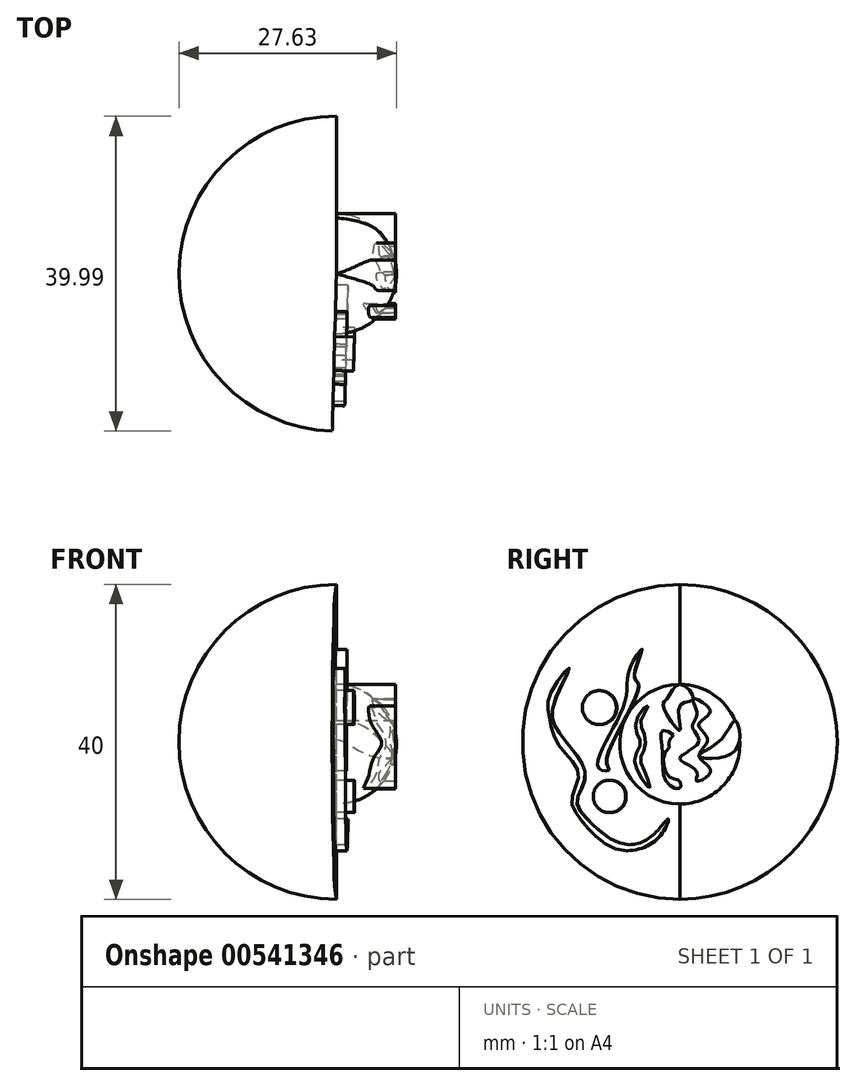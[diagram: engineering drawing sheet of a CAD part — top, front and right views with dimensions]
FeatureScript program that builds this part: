
annotation { "Feature Type Name" : "Feature", "Feature Type Description" : "" }
export const myFeature = defineFeature(function(context is Context, id is Id, definition is map)
    precondition{}
    {
        {
            var Q0;
            Q0=qCreatedBy(makeId("Right.planeOp"),FACE);
            var sketch = newSketch(context, id + "F0", { "sketchPlane" : qUnion([Q0])});
            skLineSegment(sketch, "E0", {"start": v(0, 0) * mm, "end": v(0, 40) * mm});
            skArc(sketch, "E1", {"start": v(0, 40) * mm, "mid": v(20, 20) * mm, "end": v(0, 0) * mm});
            skSolve(sketch);
        }
        {
            var Q0;
            Q0 = qSketchRegion(id + "F0", true);
            var Q1;
            Q1=sQuery(id+"F0.wireOp",EDGE,"E0");
            revolve(context, id + "F1", {"entities" : qUnion([Q0]), "axis" : qUnion([Q1]), "revolveType" : RevolveType.ONE_DIRECTION, "angle" : 178.48 * degree});
        }
        {
            var Q0;
            Q0=makeQuery(id+"F1.opRevolve","CAP_FACE",FACE,{"disambiguationData":[OSD([sQuery(id+"F0.wireOp",EDGE,"E0"),sQuery(id+"F0.wireOp",EDGE,"E1")])],"isStart":true});
            var sketch = newSketch(context, id + "F2", { "sketchPlane" : qUnion([Q0])});
            skLineSegment(sketch, "E2", {"start": v(0, 12.12) * mm, "end": v(0, 27.3) * mm});
            skArc(sketch, "E3", {"start": v(0, 12.12) * mm, "mid": v(7.63, 19.71) * mm, "end": v(0, 27.3) * mm});
            skSolve(sketch);
        }
        {
            var Q0;
            Q0=makeQuery(id+"F2.imprint","IMPRINT",FACE,{"disambiguationData":[TD([[makeQuery(id+"F2.imprint","IMPRINT",EDGE,{"derivedFrom":sQuery(id+"F2.wireOp",EDGE,"E2")}),-1.0]])]});
            var Q1;
            Q1=sQuery(id+"F2.wireOp",EDGE,"E2");
            revolve(context, id + "F3", {"operationType" : NewBodyOperationType.ADD, "entities" : qUnion([Q0]), "axis" : qUnion([Q1]), "revolveType" : RevolveType.FULL});
        }
        {
            var Q0;
            Q0=makeQuery(id+"F1.opRevolve","CAP_FACE",FACE,{"disambiguationData":[OSD([sQuery(id+"F0.wireOp",EDGE,"E0"),sQuery(id+"F0.wireOp",EDGE,"E1")])],"isStart":false});
            var sketch = newSketch(context, id + "F4", { "sketchPlane" : qUnion([Q0])});
            skCircle(sketch, "E4", {"center": v(-8.87, 13.08) * mm, "radius": 2.06 * mm});
            skSolve(sketch);
        }
        {
            var Q0;
            Q0=makeQuery(id+"F4.imprint","IMPRINT",FACE,{"disambiguationData":[TD([[makeQuery(id+"F4.imprint","IMPRINT",EDGE,{"derivedFrom":sQuery(id+"F4.wireOp",EDGE,"E4")}),1.0]])]});
            extrude(context, id + "F5", {"entities" : qUnion([Q0]), "operationType" : NewBodyOperationType.ADD, "depth" : 2.5 * mm, "offsetDistance" : 25 * mm});
        }
        {
            var Q0;
            Q0=makeQuery(id+"F1.opRevolve","CAP_FACE",FACE,{"disambiguationData":[OSD([sQuery(id+"F0.wireOp",EDGE,"E0"),sQuery(id+"F0.wireOp",EDGE,"E1")])],"isStart":false});
            var sketch = newSketch(context, id + "F6", { "sketchPlane" : qUnion([Q0])});
            skCircle(sketch, "E5", {"center": v(-10.16, 24.36) * mm, "radius": 2.16 * mm});
            skSolve(sketch);
        }
        {
            var Q0;
            Q0=makeQuery(id+"F6.imprint","IMPRINT",FACE,{"disambiguationData":[TD([[makeQuery(id+"F6.imprint","IMPRINT",EDGE,{"derivedFrom":sQuery(id+"F6.wireOp",EDGE,"E5")}),1.0]])]});
            extrude(context, id + "F7", {"entities" : qUnion([Q0]), "operationType" : NewBodyOperationType.ADD, "depth" : 2.5 * mm, "offsetDistance" : 25 * mm});
        }
        {
            var Q0;
            Q0=makeQuery(id+"F1.opRevolve","CAP_FACE",FACE,{"disambiguationData":[OSD([sQuery(id+"F0.wireOp",EDGE,"E0"),sQuery(id+"F0.wireOp",EDGE,"E1")])],"isStart":true});
            var sketch = newSketch(context, id + "F8", { "sketchPlane" : qUnion([Q0])});
            skFitSpline(sketch, "E6", {"points": [v(1.7, 25.46) * mm, v(3.87, 23.89) * mm, v(2.4, 22.22) * mm, v(3.52, 20.3) * mm, v(2.44, 18.2) * mm, v(3.92, 16.28) * mm, v(2.15, 15) * mm, v(2.15, 16.23) * mm, v(0, 17.9) * mm, v(2.4, 19.96) * mm, v(1.6, 21.92) * mm, v(2.2, 23.6) * mm, v(1.7, 25.46) * mm]});
            skFitSpline(sketch, "E7", {"points": [v(-4.04, 24.58) * mm, v(-5.22, 23.45) * mm, v(-5.46, 21.19) * mm, v(-4.97, 19.81) * mm, v(-5.7, 18.1) * mm, v(-4.92, 15.54) * mm, v(-3.84, 14.12) * mm, v(-4.24, 15.74) * mm, v(-5.02, 17.85) * mm, v(-4.48, 19.08) * mm, v(-4.58, 21.19) * mm, v(-4.92, 22.66) * mm, v(-4.04, 24.58) * mm]});
            skFitSpline(sketch, "E8", {"points": [v(-2.12, 21.43) * mm, v(0, 20) * mm, v(-1.58, 19.08) * mm, v(-1.48, 15.74) * mm, v(0, 15) * mm, v(0, 14.12) * mm, v(-1.73, 15) * mm, v(-2.22, 19.08) * mm, v(-2.12, 21.43) * mm]});
            skFitSpline(sketch, "E9", {"points": [v(-1.58, 25.5) * mm, v(-2.12, 24.58) * mm, v(0, 21.43) * mm, v(0, 24.58) * mm, v(1.7, 25.46) * mm, v(0, 27.3) * mm, v(-1.58, 25.5) * mm]});
            skFitSpline(sketch, "E10", {"points": [v(5.64, 18.1) * mm, v(7.6, 20.3) * mm, v(7.03, 22.66) * mm, v(5.24, 20.3) * mm, v(2.44, 18.2) * mm, v(5.64, 18.1) * mm]});
            skSolve(sketch);
        }
        {
            var Q0;
            Q0 = qSketchRegion(id + "F8", true);
            extrude(context, id + "F9", {"entities" : qUnion([Q0]), "operationType" : NewBodyOperationType.ADD, "depth" : 7.5 * mm, "offsetDistance" : 25 * mm});
        }
        {
            var Q0;
            Q0=makeQuery(id+"F1.opRevolve","CAP_FACE",FACE,{"disambiguationData":[OSD([sQuery(id+"F0.wireOp",EDGE,"E0"),sQuery(id+"F0.wireOp",EDGE,"E1")])],"isStart":false});
            var sketch = newSketch(context, id + "F10", { "sketchPlane" : qUnion([Q0])});
            skFitSpline(sketch, "E11", {"points": [v(-14.06, 29.35) * mm, v(-16.41, 26.13) * mm, v(-16.56, 23.21) * mm, v(-15.3, 19.54) * mm, v(-12.82, 16.06) * mm, v(-13.68, 12.62) * mm, v(-12.15, 9.67) * mm, v(-7.88, 6.33) * mm, v(-2.6, 7.9) * mm, v(-1.48, 10.19) * mm, v(-3.54, 8.02) * mm, v(-7.54, 7.12) * mm, v(-11.44, 9.89) * mm, v(-13.05, 12.43) * mm, v(-12, 15.46) * mm, v(-13.23, 18.5) * mm, v(-15.52, 21.49) * mm, v(-16.08, 24.52) * mm, v(-14.06, 29.35) * mm]});
            skSolve(sketch);
        }
        {
            var Q0;
            Q0=makeQuery(id+"F10.imprint","IMPRINT",FACE,{"disambiguationData":[TD([[makeQuery(id+"F10.imprint","IMPRINT",EDGE,{"derivedFrom":sQuery(id+"F10.wireOp",EDGE,"E11")}),1.0]])]});
            extrude(context, id + "F11", {"entities" : qUnion([Q0]), "operationType" : NewBodyOperationType.ADD, "depth" : 1.5 * mm, "offsetDistance" : 25 * mm});
        }
        {
            var Q0;
            Q0=makeQuery(id+"F1.opRevolve","CAP_FACE",FACE,{"disambiguationData":[OSD([sQuery(id+"F0.wireOp",EDGE,"E0"),sQuery(id+"F0.wireOp",EDGE,"E1")])],"isStart":false});
            var sketch = newSketch(context, id + "F12", { "sketchPlane" : qUnion([Q0])});
            skPoint(sketch, "E12.3.internal.snap0", {"position": v(-7.63, 19.71) * mm});
            skFitSpline(sketch, "E12", {"points": [v(-4.8, 31.74) * mm, v(-6.29, 29.4) * mm, v(-6.84, 25.44) * mm, v(-9.52, 19.71) * mm, v(-10.18, 16.57) * mm, v(-8.99, 16.4) * mm, v(-9.29, 17.53) * mm, v(-5.18, 27.07) * mm, v(-5.75, 28.3) * mm, v(-4.8, 31.74) * mm]});
            skSolve(sketch);
        }
        {
            var Q0;
            Q0 = qSketchRegion(id + "F12", true);
            extrude(context, id + "F13", {"entities" : qUnion([Q0]), "operationType" : NewBodyOperationType.ADD, "depth" : 1.5 * mm, "offsetDistance" : 25 * mm});
        }
    });
